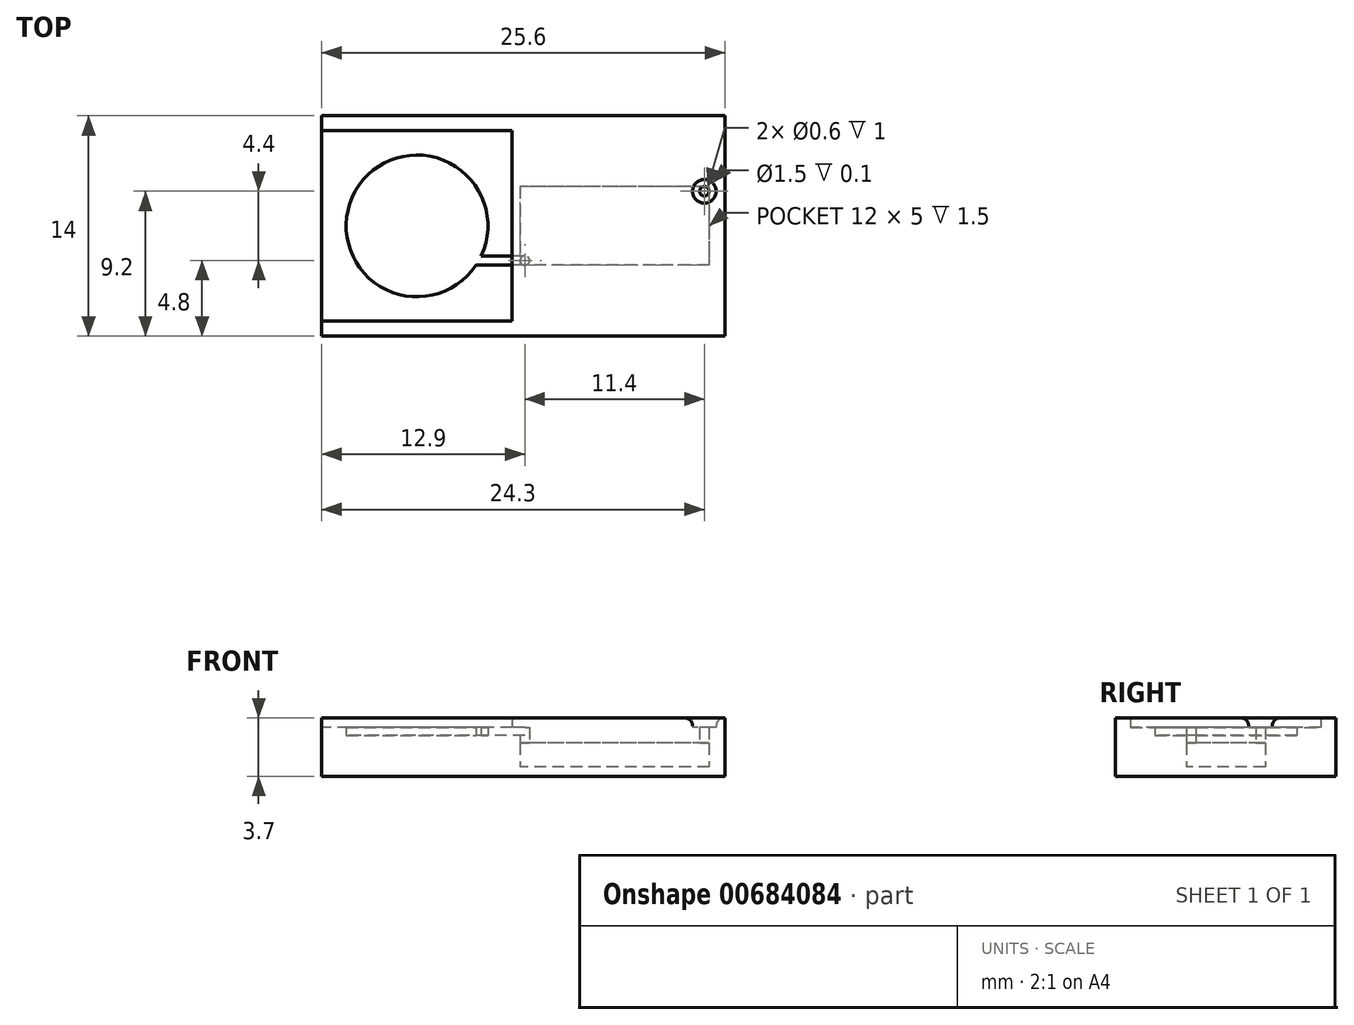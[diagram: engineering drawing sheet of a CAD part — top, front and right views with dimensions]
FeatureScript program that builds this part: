
annotation { "Feature Type Name" : "Feature", "Feature Type Description" : "" }
export const myFeature = defineFeature(function(context is Context, id is Id, definition is map)
    precondition{}
    {
        {
            var Q0;
            Q0=qCreatedBy(makeId("Top.planeOp"),FACE);
            var sketch = newSketch(context, id + "F0", { "sketchPlane" : qUnion([Q0])});
            skLineSegment(sketch, "E0.bottom", {"start": v(6, 2.5) * mm, "end": v(-6, 2.5) * mm});
            skLineSegment(sketch, "E0.top", {"start": v(6, -2.5) * mm, "end": v(-6, -2.5) * mm});
            skLineSegment(sketch, "E0.left", {"start": v(6, 2.5) * mm, "end": v(6, -2.5) * mm});
            skLineSegment(sketch, "E0.right", {"start": v(-6, 2.5) * mm, "end": v(-6, -2.5) * mm});
            skPoint(sketch, "E0.middle", {"position": v(0, 0) * mm});
            skLineSegment(sketch, "E1", {"start": v(6, 2.5) * mm, "end": v(6, 2.2) * mm, "construction": true});
            skLineSegment(sketch, "E2", {"start": v(6, 2.5) * mm, "end": v(5.7, 2.5) * mm, "construction": true});
            skLineSegment(sketch, "E3", {"start": v(-6, -2.5) * mm, "end": v(-5.7, -2.5) * mm, "construction": true});
            skLineSegment(sketch, "E4", {"start": v(-6, -2.5) * mm, "end": v(-6, -2.2) * mm, "construction": true});
            skCircle(sketch, "E5", {"center": v(5.7, 2.2) * mm, "radius": 0.3 * mm});
            skCircle(sketch, "E6", {"center": v(-5.7, -2.2) * mm, "radius": 0.3 * mm});
            skCircle(sketch, "E7", {"center": v(-12.55, 0) * mm, "radius": 4.5 * mm});
            skLineSegment(sketch, "E8", {"start": v(-12.55, 0) * mm, "end": v(-12.55, -6.05) * mm, "construction": true});
            skLineSegment(sketch, "E9", {"start": v(-12.55, 0) * mm, "end": v(-18.6, 0) * mm, "construction": true});
            skLineSegment(sketch, "E10", {"start": v(-12.55, 0) * mm, "end": v(-12.55, 6.05) * mm, "construction": true});
            skLineSegment(sketch, "E11", {"start": v(-12.55, 0) * mm, "end": v(-6.5, 0) * mm, "construction": true});
            skLineSegment(sketch, "E12", {"start": v(-6.5, 0) * mm, "end": v(-6, 0) * mm, "construction": true});
            skLineSegment(sketch, "E13", {"start": v(-18.6, 6.05) * mm, "end": v(-18.6, -6.05) * mm});
            skLineSegment(sketch, "E14", {"start": v(-18.6, -6.05) * mm, "end": v(-6.5, -6.05) * mm});
            skLineSegment(sketch, "E15", {"start": v(-6.5, -6.05) * mm, "end": v(-6.5, 6.05) * mm});
            skLineSegment(sketch, "E16", {"start": v(-6.5, 6.05) * mm, "end": v(-18.6, 6.05) * mm});
            skLineSegment(sketch, "E17", {"start": v(-5.7, -1.9) * mm, "end": v(-12.55, -1.9) * mm, "construction": true});
            skLineSegment(sketch, "E18", {"start": v(-5.7, -2.5) * mm, "end": v(-12.55, -2.5) * mm, "construction": true});
            skLineSegment(sketch, "E19", {"start": v(6, -2.5) * mm, "end": v(6, -7) * mm, "construction": true});
            skLineSegment(sketch, "E20", {"start": v(6, 2.5) * mm, "end": v(6, 7) * mm, "construction": true});
            skLineSegment(sketch, "E21", {"start": v(6, -7) * mm, "end": v(7, -7) * mm, "construction": true});
            skLineSegment(sketch, "E22", {"start": v(7, -7) * mm, "end": v(-18.6, -7) * mm});
            skLineSegment(sketch, "E23", {"start": v(-18.6, -7) * mm, "end": v(-18.6, -6.05) * mm});
            skLineSegment(sketch, "E24", {"start": v(-18.6, 6.05) * mm, "end": v(-18.6, 7) * mm});
            skLineSegment(sketch, "E25", {"start": v(-18.6, 7) * mm, "end": v(7, 7) * mm});
            skLineSegment(sketch, "E26", {"start": v(7, 7) * mm, "end": v(7, -7) * mm});
            skSolve(sketch);
        }
        {
            var Q0;
            Q0=makeQuery(id+"F0.imprint","IMPRINT",FACE,{"disambiguationData":[TD([[makeQuery(id+"F0.imprint","IMPRINT",EDGE,{"derivedFrom":sQuery(id+"F0.wireOp",EDGE,"E14")}),-1.0]])]});
            var sketch = newSketch(context, id + "F1", { "sketchPlane" : qUnion([Q0])});
            skLineSegment(sketch, "E27.0", {"start": v(-18.6, 7) * mm, "end": v(7, 7) * mm});
            skLineSegment(sketch, "E28.0", {"start": v(-18.6, 6.05) * mm, "end": v(-18.6, 7) * mm});
            skLineSegment(sketch, "E28.1", {"start": v(-18.6, 6.05) * mm, "end": v(-18.6, -6.05) * mm});
            skLineSegment(sketch, "E28.2", {"start": v(-18.6, -7) * mm, "end": v(-18.6, -6.05) * mm});
            skLineSegment(sketch, "E28.3", {"start": v(7, -7) * mm, "end": v(-18.6, -7) * mm});
            skLineSegment(sketch, "E28.4", {"start": v(7, 7) * mm, "end": v(7, -7) * mm});
            skSolve(sketch);
        }
        {
            var Q0;
            Q0 = qSketchRegion(id + "F1", true);
            extrude(context, id + "F2", {"entities" : qUnion([Q0]), "depth" : .6 * mm, "offsetDistance" : 25 * mm});
        }
        {
            var Q0;
            Q0=makeQuery(id+"F2.opExtrude","CAP_FACE",FACE,{"disambiguationData":[OSD([sQuery(id+"F1.wireOp",EDGE,"E27.0"),sQuery(id+"F1.wireOp",EDGE,"E28.0"),sQuery(id+"F1.wireOp",EDGE,"E28.1"),sQuery(id+"F1.wireOp",EDGE,"E28.2"),sQuery(id+"F1.wireOp",EDGE,"E28.3"),sQuery(id+"F1.wireOp",EDGE,"E28.4")])],"isStart":false});
            var sketch = newSketch(context, id + "F3", { "sketchPlane" : qUnion([Q0])});
            skLineSegment(sketch, "E29.0", {"start": v(-18.6, 7) * mm, "end": v(7, 7) * mm});
            skLineSegment(sketch, "E29.1", {"start": v(7, 7) * mm, "end": v(7, -7) * mm});
            skLineSegment(sketch, "E29.2", {"start": v(7, -7) * mm, "end": v(-18.6, -7) * mm});
            skLineSegment(sketch, "E29.3", {"start": v(-18.6, -7) * mm, "end": v(-18.6, -6.05) * mm});
            skLineSegment(sketch, "E29.4", {"start": v(-18.6, 6.05) * mm, "end": v(-18.6, -6.05) * mm});
            skLineSegment(sketch, "E29.5", {"start": v(-18.6, 6.05) * mm, "end": v(-18.6, 7) * mm});
            skLineSegment(sketch, "E29.6", {"start": v(6, 2.5) * mm, "end": v(-6, 2.5) * mm});
            skLineSegment(sketch, "E29.7", {"start": v(-6, 2.5) * mm, "end": v(-6, -2.5) * mm});
            skLineSegment(sketch, "E29.8", {"start": v(6, -2.5) * mm, "end": v(-6, -2.5) * mm});
            skLineSegment(sketch, "E29.9", {"start": v(6, 2.5) * mm, "end": v(6, -2.5) * mm});
            skSolve(sketch);
        }
        {
            var Q0;
            Q0 = qSketchRegion(id + "F3", true);
            extrude(context, id + "F4", {"entities" : qUnion([Q0]), "operationType" : NewBodyOperationType.ADD, "depth" : 1.5 * mm, "offsetDistance" : 25 * mm});
        }
        {
            var Q0;
            Q0=makeQuery(id+"F4.opExtrude","CAP_FACE",FACE,{"disambiguationData":[OSD([sQuery(id+"F3.wireOp",EDGE,"E29.0"),sQuery(id+"F3.wireOp",EDGE,"E29.1"),sQuery(id+"F3.wireOp",EDGE,"E29.2"),sQuery(id+"F3.wireOp",EDGE,"E29.3"),sQuery(id+"F3.wireOp",EDGE,"E29.4"),sQuery(id+"F3.wireOp",EDGE,"E29.5"),sQuery(id+"F3.wireOp",EDGE,"E29.6"),sQuery(id+"F3.wireOp",EDGE,"E29.7"),sQuery(id+"F3.wireOp",EDGE,"E29.8"),sQuery(id+"F3.wireOp",EDGE,"E29.9")])],"isStart":false});
            var sketch = newSketch(context, id + "F5", { "sketchPlane" : qUnion([Q0])});
            skCircle(sketch, "E30.0", {"center": v(-5.7, -2.2) * mm, "radius": 0.3 * mm});
            skCircle(sketch, "E30.1", {"center": v(5.7, 2.2) * mm, "radius": 0.3 * mm});
            skLineSegment(sketch, "E31.0", {"start": v(-18.6, 7) * mm, "end": v(7, 7) * mm});
            skLineSegment(sketch, "E31.1", {"start": v(7, 7) * mm, "end": v(7, -7) * mm});
            skPoint(sketch, "E31.2", {"position": v(6, -7) * mm});
            skLineSegment(sketch, "E31.3", {"start": v(7, -7) * mm, "end": v(-18.6, -7) * mm});
            skLineSegment(sketch, "E31.4", {"start": v(-18.6, -7) * mm, "end": v(-18.6, -6.05) * mm});
            skLineSegment(sketch, "E31.5", {"start": v(-18.6, 6.05) * mm, "end": v(-18.6, -6.05) * mm});
            skLineSegment(sketch, "E31.6", {"start": v(-18.6, 6.05) * mm, "end": v(-18.6, 7) * mm});
            skSolve(sketch);
        }
        {
            var Q0;
            Q0 = qSketchRegion(id + "F5", true);
            extrude(context, id + "F6", {"entities" : qUnion([Q0]), "operationType" : NewBodyOperationType.ADD, "depth" : .5 * mm, "offsetDistance" : 25 * mm});
        }
        {
            var Q0;
            Q0=makeQuery(id+"F6.opExtrude","CAP_FACE",FACE,{"disambiguationData":[OSD([sQuery(id+"F5.wireOp",EDGE,"E30.0"),sQuery(id+"F5.wireOp",EDGE,"E30.1"),sQuery(id+"F5.wireOp",EDGE,"E31.0"),sQuery(id+"F5.wireOp",EDGE,"E31.1"),sQuery(id+"F5.wireOp",EDGE,"E31.3"),sQuery(id+"F5.wireOp",EDGE,"E31.4"),sQuery(id+"F5.wireOp",EDGE,"E31.5"),sQuery(id+"F5.wireOp",EDGE,"E31.6")])],"isStart":false});
            var sketch = newSketch(context, id + "F7", { "sketchPlane" : qUnion([Q0])});
            skLineSegment(sketch, "E32.0", {"start": v(-18.6, 7) * mm, "end": v(7, 7) * mm});
            skLineSegment(sketch, "E32.1", {"start": v(-18.6, 6.05) * mm, "end": v(-18.6, 7) * mm});
            skLineSegment(sketch, "E32.2", {"start": v(-18.6, 6.05) * mm, "end": v(-18.6, -6.05) * mm});
            skLineSegment(sketch, "E32.3", {"start": v(-18.6, -7) * mm, "end": v(-18.6, -6.05) * mm});
            skLineSegment(sketch, "E32.4", {"start": v(7, -7) * mm, "end": v(-18.6, -7) * mm});
            skLineSegment(sketch, "E32.5", {"start": v(7, 7) * mm, "end": v(7, -7) * mm});
            skCircle(sketch, "E32.6", {"center": v(5.7, 2.2) * mm, "radius": 0.3 * mm});
            skCircle(sketch, "E32.7", {"center": v(-5.7, -2.2) * mm, "radius": 0.3 * mm});
            skLineSegment(sketch, "E32.8", {"start": v(-5.7, -1.9) * mm, "end": v(-12.55, -1.9) * mm});
            skLineSegment(sketch, "E32.9", {"start": v(-5.7, -2.5) * mm, "end": v(-12.55, -2.5) * mm});
            skCircle(sketch, "E32.10", {"center": v(-12.55, 0) * mm, "radius": 4.5 * mm});
            skSolve(sketch);
        }
        {
            var Q0;
            Q0 = qSketchRegion(id + "F7", true);
            extrude(context, id + "F8", {"entities" : qUnion([Q0]), "operationType" : NewBodyOperationType.ADD, "depth" : .5 * mm, "offsetDistance" : 25 * mm});
        }
        {
            var Q0;
            Q0=makeQuery(id+"F8.opExtrude","CAP_FACE",FACE,{"disambiguationData":[OSD([sQuery(id+"F7.wireOp",EDGE,"E32.0"),sQuery(id+"F7.wireOp",EDGE,"E32.1"),sQuery(id+"F7.wireOp",EDGE,"E32.2"),sQuery(id+"F7.wireOp",EDGE,"E32.3"),sQuery(id+"F7.wireOp",EDGE,"E32.4"),sQuery(id+"F7.wireOp",EDGE,"E32.5"),sQuery(id+"F7.wireOp",EDGE,"E32.6"),sQuery(id+"F7.wireOp",EDGE,"E32.7"),sQuery(id+"F7.wireOp",EDGE,"E32.8"),sQuery(id+"F7.wireOp",EDGE,"E32.9"),sQuery(id+"F7.wireOp",EDGE,"E32.10")])],"isStart":false});
            var sketch = newSketch(context, id + "F9", { "sketchPlane" : qUnion([Q0])});
            skLineSegment(sketch, "E33.0", {"start": v(-18.6, 7) * mm, "end": v(7, 7) * mm});
            skLineSegment(sketch, "E33.1", {"start": v(-18.6, 6.05) * mm, "end": v(-18.6, 7) * mm});
            skLineSegment(sketch, "E33.3", {"start": v(-18.6, -7) * mm, "end": v(-18.6, -6.05) * mm});
            skLineSegment(sketch, "E33.4", {"start": v(7, -7) * mm, "end": v(-18.6, -7) * mm});
            skLineSegment(sketch, "E33.5", {"start": v(7, 7) * mm, "end": v(7, -7) * mm});
            skCircle(sketch, "E33.6", {"center": v(5.7, 2.2) * mm, "radius": 0.3 * mm, "construction": true});
            skLineSegment(sketch, "E33.7", {"start": v(-6.5, 6.05) * mm, "end": v(-18.6, 6.05) * mm});
            skLineSegment(sketch, "E33.8", {"start": v(-6.5, -6.05) * mm, "end": v(-6.5, 6.05) * mm});
            skLineSegment(sketch, "E33.9", {"start": v(-18.6, -6.05) * mm, "end": v(-6.5, -6.05) * mm});
            skCircle(sketch, "E34", {"center": v(5.7, 2.2) * mm, "radius": 0.75 * mm});
            skSolve(sketch);
        }
        {
            var Q0;
            Q0 = qSketchRegion(id + "F9", true);
            extrude(context, id + "F10", {"entities" : qUnion([Q0]), "operationType" : NewBodyOperationType.ADD, "depth" : .6 * mm, "offsetDistance" : 25 * mm});
        }
        {
            var Q0;
            Q0=makeQuery(id+"F10.opExtrude","CAP_EDGE",EDGE,{"disambiguationData":[OSD([sQuery(id+"F9.wireOp",EDGE,"E34")])],"isStart":false});
            fillet(context, id + "F11", {"entities" : qUnion([Q0]), "radius" : .5 * mm, "tangentPropagation" : true, "allowEdgeOverflow" : false});
        }
    });
